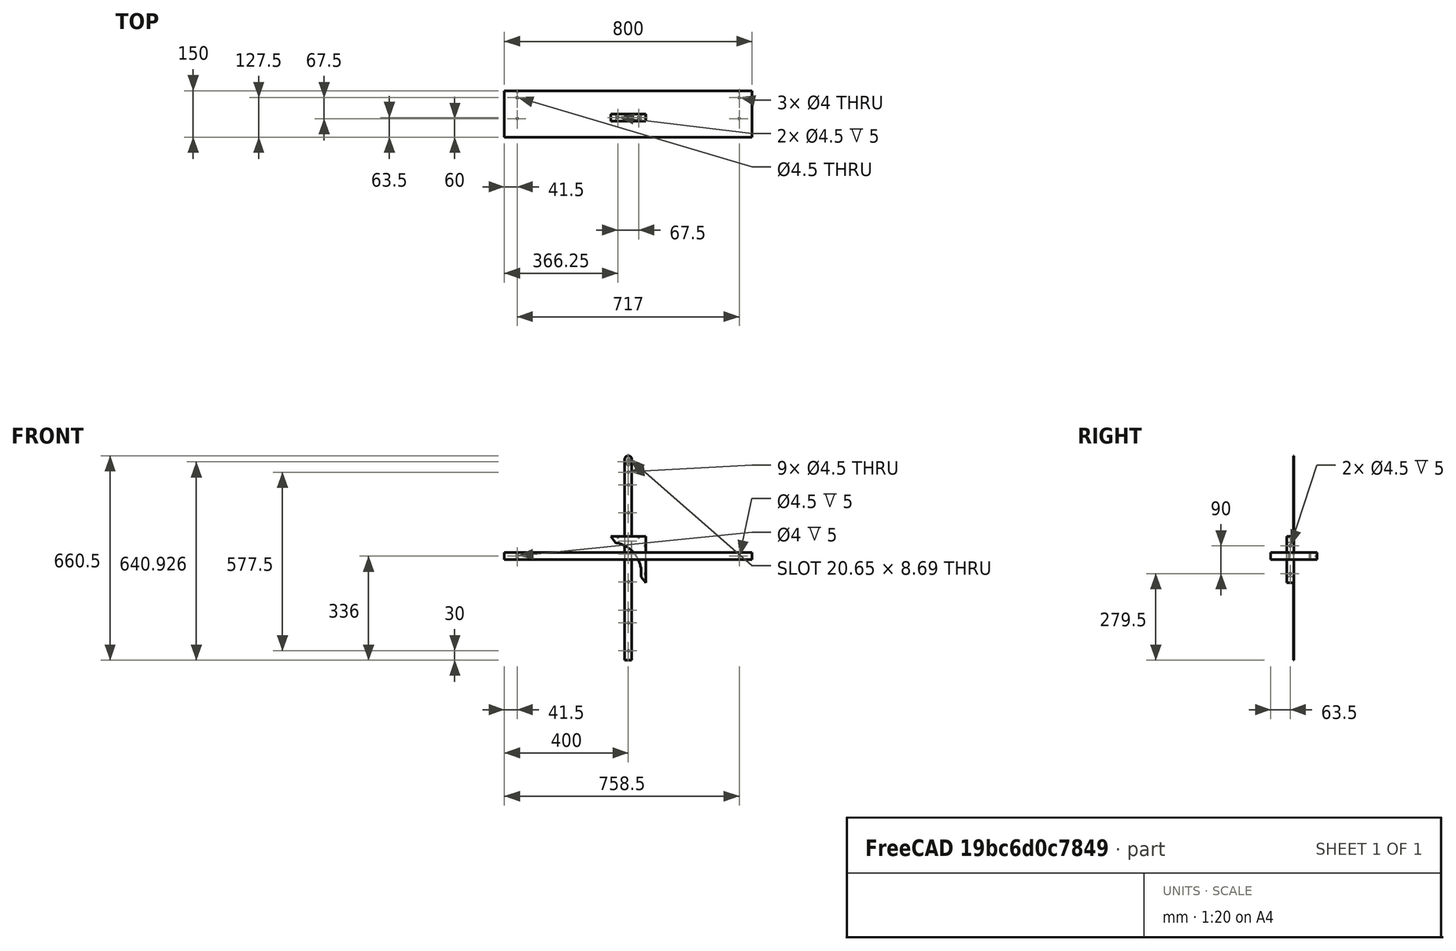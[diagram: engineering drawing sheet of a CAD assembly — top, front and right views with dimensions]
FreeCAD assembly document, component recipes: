
FREECAD ASSEMBLY — COMPONENT RECIPES ("shelf")

This assembly document has 11 components, labeled P0..P10 below (a component is one placed body or linked part). 11 of them carry a construction recipe — the FreeCAD feature program that regenerates the part from scratch, quoted from this document or its linked companion documents; the rest are supplied as boundary geometry only. No exploded tour is included for this assembly.
COMPONENT P0 — recipe-attached ("Plank001", modeled in this document).
Construction recipe (the document's own serialized feature program — sketch geometry with constraints, then the solid features built on it; lengths are millimeters unless a unit is written):

FEATURE [Sketcher::SketchObject] Sketch  label="Top view"
  ArcFitTolerance = 1e-06
  AttachmentSupport = -> [XY_Plane]
  FullyConstrained = true
  MakeInternals = false
  MapMode = 5
  expr: Constraints[12] = <<data>>.pw
  expr: Constraints[13] = <<data>>.pl
  sketch-geometry (6):
    g0: LineSegment StartX=400 StartY=-75 StartZ=0 EndX=400 EndY=75 EndZ=0
    g1: LineSegment StartX=400 StartY=75 StartZ=0 EndX=-400 EndY=75 EndZ=0
    g2: LineSegment StartX=-400 StartY=75 StartZ=0 EndX=-400 EndY=-75 EndZ=0
    g3: LineSegment StartX=-400 StartY=-75 StartZ=0 EndX=400 EndY=-75 EndZ=0
    g4: GeomPoint [constr] X=-2.3e-15 Y=75 Z=0
    g5: GeomPoint [constr] X=400 Y=0 Z=0
  constraints (14):
    c: Coincident(g0,g1)
    c: Coincident(g1,g2)
    c: Coincident(g2,g3)
    c: Coincident(g3,g0)
    c: Vertical(g0)
    c: Vertical(g2)
    c: Horizontal(g1)
    c: Horizontal(g3)
    c: Symmetric(g1,g1,g4)
    c: Symmetric(g0,g0,g5)
    c: Vertical(g4,g-1)
    c: Horizontal(g5,g-1)
    c: DistanceY(g2,g2) = 150
    c: DistanceX(g3,g3) = 800
FEATURE [PartDesign::Pad] Pad
  Direction = (0,0,1)
  Length = 23
  Length2 = 10
  Profile = -> Sketch
  ReferenceAxis = -> Sketch [N_Axis]
  Refine = true
  Suppressed = false
  Type = 0
  expr: Length = <<data>>.pt
FEATURE [Sketcher::SketchObject] Sketch005
  ArcFitTolerance = 1e-06
  AttachmentSupport = -> [Pad]
  ExternalGeometry = -> [Pad]
  FullyConstrained = true
  MakeInternals = false
  MapMode = 5
  Placement = pos=(0,0,23) rot=(0,0,1;0rad)
  expr: Constraints[22] = <<data>>.pw * <<data>>.tr * <<data>>.hr
  expr: Constraints[24] = <<data>>.pw - <<data>>.pw * <<data>>.tr * (1 - <<data>>.hr)
  expr: Constraints[25] = <<data>>.pt / 2 + <<data>>.ts
  expr: Constraints[6] = <<data>>.sd
  sketch-geometry (11):
    g0: GeomPoint [constr] X=-358.5 Y=75 Z=0
    g1: GeomPoint [constr] X=-358.5 Y=-75 Z=0
    g2: LineSegment [constr] StartX=-358.5 StartY=75 StartZ=0 EndX=-358.5 EndY=-75 EndZ=0
    g3: Circle CenterX=-358.5 CenterY=52.5 CenterZ=0 NormalX=0 NormalY=0 NormalZ=1 AngleXU=0 Radius=2.25
    g4: LineSegment [constr] StartX=-400 StartY=75 StartZ=0 EndX=-400 EndY=52.5 EndZ=0
    g5: LineSegment [constr] StartX=-400 StartY=52.5 StartZ=0 EndX=-358.5 EndY=52.5 EndZ=0
    g6: LineSegment [constr] StartX=-358.5 StartY=52.5 StartZ=0 EndX=-358.5 EndY=75 EndZ=0
    g7: LineSegment [constr] StartX=-358.5 StartY=75 StartZ=0 EndX=-400 EndY=75 EndZ=0
    g8: Circle CenterX=-358.5 CenterY=-15 CenterZ=0 NormalX=0 NormalY=0 NormalZ=1 AngleXU=0 Radius=2
    g9: Circle CenterX=358.5 CenterY=-15 CenterZ=0 NormalX=0 NormalY=0 NormalZ=1 AngleXU=0 Radius=2
    g10: Circle CenterX=358.5 CenterY=52.5 CenterZ=0 NormalX=0 NormalY=0 NormalZ=1 AngleXU=0 Radius=2
  constraints (26):
    c: PointOnObject(g0,g-3)
    c: PointOnObject(g1,g-5)
    c: Coincident(g2,g0)
    c: Coincident(g2,g1)
    c: Vertical(g2)
    c: PointOnObject(g3,g2)
    c: Diameter(g3) = 4.5
    c: Coincident(g4,g5)
    c: Coincident(g5,g6)
    c: Coincident(g6,g7)
    c: Coincident(g7,g4)
    c: Vertical(g4)
    c: Vertical(g6)
    c: Horizontal(g5)
    c: Horizontal(g7)
    c: Coincident(g4,g-4)
    c: Coincident(g5,g3)
    c: Diameter(g8) = 4
    c: Diameter(g9) = 4
    c: Symmetric(g9,g8,g-2)
    c: Diameter(g10) = 4
    c: Symmetric(g10,g3,g-2)
    c: DistanceY(g3,g0) = 22.5
    c: PointOnObject(g8,g2)
    c: DistanceY(g-5,g8) = 60
    c: Distance(g5,g5) = 41.5
FEATURE [PartDesign::Pocket] Pocket002
  BaseFeature = -> Pad
  Direction = (0,0,-1)
  Length = 23
  Length2 = 5
  Profile = -> Sketch005
  ReferenceAxis = -> Sketch005 [N_Axis]
  Refine = true
  Suppressed = false
  Type = 0
  expr: Length = <<data>>.pt
FEATURE [Sketcher::SketchObject] Sketch006
  ArcFitTolerance = 1e-06
  AttachmentSupport = -> [Pocket002]
  ExternalGeometry = -> [Pocket002]
  FullyConstrained = true
  MakeInternals = false
  MapMode = 5
  Placement = pos=(0,75,0) rot=(0,0.707107,0.707107;3.14159rad)
  expr: Constraints[11] = <<data>>.sd
  expr: Constraints[14] = <<data>>.pt / 2
  expr: Constraints[9] = <<data>>.pt / 2 + <<data>>.ts
  sketch-geometry (6):
    g0: LineSegment [constr] StartX=-400 StartY=23 StartZ=0 EndX=-400 EndY=11.5 EndZ=0
    g1: LineSegment [constr] StartX=-400 StartY=11.5 StartZ=0 EndX=-358.5 EndY=11.5 EndZ=0
    g2: LineSegment [constr] StartX=-358.5 StartY=11.5 StartZ=0 EndX=-358.5 EndY=23 EndZ=0
    g3: LineSegment [constr] StartX=-358.5 StartY=23 StartZ=0 EndX=-400 EndY=23 EndZ=0
    g4: Circle CenterX=-358.5 CenterY=11.5 CenterZ=0 NormalX=0 NormalY=0 NormalZ=1 AngleXU=0 Radius=2.25
    g5: Circle CenterX=358.5 CenterY=11.5 CenterZ=0 NormalX=0 NormalY=0 NormalZ=1 AngleXU=0 Radius=2
  constraints (15):
    c: Coincident(g0,g1)
    c: Coincident(g1,g2)
    c: Coincident(g2,g3)
    c: Coincident(g3,g0)
    c: Vertical(g0)
    c: Vertical(g2)
    c: Horizontal(g1)
    c: Horizontal(g3)
    c: Coincident(g0,g-4)
    c: DistanceX(g3,g3) = 41.5
    c: Coincident(g4,g1)
    c: Diameter(g4) = 4.5
    c: Diameter(g5) = 4
    c: Symmetric(g1,g5,g-2)
    c: DistanceY(g0,g0) = 11.5
FEATURE [PartDesign::Pocket] Pocket003
  BaseFeature = -> Pocket002
  Direction = (0,-1,2e-16)
  Length = 5
  Length2 = 5
  Profile = -> Sketch006
  ReferenceAxis = -> Sketch006 [N_Axis]
  Refine = true
  Suppressed = false
  Type = 0
FEATURE [PartDesign::Body] Body  label="Plank"
  AllowCompound = false
  Group = -> [Sketch,Pad,Sketch005,Pocket002,Sketch006,Pocket003]
  Origin = -> Origin
  Tip = -> Pocket003
COMPONENT P1 — same part as P0; its construction recipe is shown at P0.
COMPONENT P2 — same part as P0; its construction recipe is shown at P0.
COMPONENT P3 — recipe-attached ("Strip001", modeled in this document).
Construction recipe (the document's own serialized feature program — sketch geometry with constraints, then the solid features built on it; lengths are millimeters unless a unit is written):

FEATURE [Sketcher::SketchObject] Sketch002
  ArcFitTolerance = 1e-06
  AttachmentSupport = -> [XZ_Plane002]
  FullyConstrained = true
  MakeInternals = false
  MapMode = 5
  Placement = pos=(0,0,0) rot=(1,0,0;1.5708rad)
  expr: Constraints[10] = <<data>>.pt
  expr: Constraints[11] = <<data>>.stl + <<data>>.pt * 3 + <<data>>.ps * 2 + <<data>>.tr * <<data>>.ps
  expr: Constraints[17] = <<data>>.sd
  expr: Constraints[18] = <<data>>.stl + <<data>>.pt + <<data>>.ps * <<data>>.tr / 5
  expr: Constraints[20] = <<data>>.sd
  expr: Constraints[21] = <<data>>.thd
  expr: Constraints[23] = <<data>>.thpi
  expr: Constraints[24] = <<data>>.sd
  expr: Constraints[26] = <<data>>.sd
  expr: Constraints[27] = <<data>>.thd
  expr: Constraints[29] = <<data>>.sd
  expr: Constraints[31] = <<data>>.sd
  expr: Constraints[32] = <<data>>.thd
  expr: Constraints[33] = <<data>>.thpi
  expr: Constraints[36] = <<data>>.pt / 2 + <<data>>.ps * <<data>>.tr * <<data>>.hr
  expr: Constraints[38] = <<data>>.sd
  expr: Constraints[39] = <<data>>.pt / 2 + <<data>>.ps * <<data>>.tr * <<data>>.hr
  expr: Constraints[41] = <<data>>.sd
  expr: Constraints[42] = <<data>>.pt / 2 + <<data>>.ps * <<data>>.tr * <<data>>.hr
  expr: Constraints[46] = <<data>>.sd
  expr: Constraints[52] = <<data>>.sd
  expr: Constraints[53] = 10 mm
  sketch-geometry (20):
    g0: LineSegment StartX=-11.5 StartY=324.5 StartZ=0 EndX=-11.5 EndY=-324.5 EndZ=0
    g1: LineSegment StartX=-11.5 StartY=-324.5 StartZ=0 EndX=11.5 EndY=-324.5 EndZ=0
    g2: LineSegment StartX=11.5 StartY=-324.5 StartZ=0 EndX=11.5 EndY=324.5 EndZ=0
    g3: LineSegment [constr] StartX=11.5 StartY=324.5 StartZ=0 EndX=-11.5 EndY=324.5 EndZ=0
    g4: ArcOfCircle CenterX=-4e-16 CenterY=324.5 CenterZ=0 NormalX=0 NormalY=0 NormalZ=1 AngleXU=0 Radius=11.5 StartAngle=0 EndAngle=3.14159
    g5: GeomPoint X=-11.5 Y=0 Z=0
    g6: GeomPoint X=0 Y=-324.5 Z=0
    g7: Circle CenterX=0 CenterY=241.5 CenterZ=0 NormalX=0 NormalY=0 NormalZ=1 AngleXU=0 Radius=2.25
    g8: Circle CenterX=0 CenterY=151.5 CenterZ=0 NormalX=0 NormalY=0 NormalZ=1 AngleXU=0 Radius=2.25
    g9: Circle CenterX=0 CenterY=18.5 CenterZ=0 NormalX=0 NormalY=0 NormalZ=1 AngleXU=0 Radius=2.25
    g10: Circle CenterX=0 CenterY=-71.5 CenterZ=0 NormalX=0 NormalY=0 NormalZ=1 AngleXU=0 Radius=2.25
    g11: Circle CenterX=0 CenterY=-204.5 CenterZ=0 NormalX=0 NormalY=0 NormalZ=1 AngleXU=0 Radius=2.25
    g12: Circle CenterX=0 CenterY=-294.5 CenterZ=0 NormalX=0 NormalY=0 NormalZ=1 AngleXU=0 Radius=2.25
    g13: Circle CenterX=0 CenterY=283 CenterZ=0 NormalX=0 NormalY=0 NormalZ=1 AngleXU=0 Radius=2.25
    g14: Circle CenterX=0 CenterY=60 CenterZ=0 NormalX=0 NormalY=0 NormalZ=1 AngleXU=0 Radius=2.25
    g15: Circle CenterX=0 CenterY=-163 CenterZ=0 NormalX=0 NormalY=0 NormalZ=1 AngleXU=0 Radius=2.25
    g16: ArcOfCircle CenterX=-4e-16 CenterY=324.5 CenterZ=0 NormalX=0 NormalY=0 NormalZ=1 AngleXU=0 Radius=2.25 StartAngle=-1.15e-14 EndAngle=3.14159
    g17: LineSegment StartX=2.25 StartY=324.5 StartZ=0 EndX=2.25 EndY=314.5 EndZ=0
    g18: LineSegment StartX=-2.25 StartY=324.5 StartZ=0 EndX=-2.25 EndY=314.5 EndZ=0
    g19: ArcOfCircle CenterX=0 CenterY=310.603 CenterZ=0 NormalX=0 NormalY=0 NormalZ=1 AngleXU=0 Radius=4.5 StartAngle=2.0944 EndAngle=7.33038
  constraints (54):
    c: Coincident(g0,g1)
    c: Coincident(g1,g2)
    c: Coincident(g2,g3)
    c: Coincident(g3,g0)
    c: Vertical(g0)
    c: Vertical(g2)
    c: Horizontal(g1)
    c: Horizontal(g3)
    c: Coincident(g4,g2)
    c: Tangent(g4,g0) = -1.5708
    c: DistanceX(g1,g1) = 23
    c: DistanceY(g2,g2) = 649
    c: Symmetric(g0,g0,g5)
    c: Symmetric(g1,g1,g6)
    c: Horizontal(g5,g-1)
    c: Vertical(g6,g-1)
    c: PointOnObject(g7,g-2)
    c: Diameter(g7) = 4.5
    c: DistanceY(g7,g4) = 83
    c: PointOnObject(g8,g-2)
    c: Diameter(g8) = 4.5
    c: DistanceY(g8,g7) = 90
    c: PointOnObject(g9,g-2)
    c: DistanceY(g9,g8) = 133
    c: Diameter(g9) = 4.5
    c: PointOnObject(g10,g-2)
    c: Diameter(g10) = 4.5
    c: DistanceY(g10,g9) = 90
    c: PointOnObject(g11,g-2)
    c: Diameter(g11) = 4.5
    c: PointOnObject(g12,g-2)
    c: Diameter(g12) = 4.5
    c: DistanceY(g12,g11) = 90
    c: DistanceY(g11,g10) = 133
    c: PointOnObject(g13,g-2)
    c: Equal(g13,g7)
    c: DistanceY(g7,g13) = 41.5
    c: PointOnObject(g14,g-2)
    c: Diameter(g14) = 4.5
    c: DistanceY(g9,g14) = 41.5
    c: PointOnObject(g15,g-2)
    c: Diameter(g15) = 4.5
    c: DistanceY(g11,g15) = 41.5
    c: Tangent(g16,g17) = 1.5708
    c: Tangent(g16,g18) = -1.5708
    c: Vertical(g18)
    c: Distance(g16,g16) = 4.5
    c: Coincident(g16,g4)
    c: Vertical(g17)
    c: PointOnObject(g19,g-2)
    c: Coincident(g19,g17)
    c: Coincident(g19,g18)
    c: Radius(g19) = 4.5
    c: DistanceY(g17,g16) = 10
FEATURE [PartDesign::Pad] Pad002
  Direction = (0,-1,2e-16)
  Length = 2
  Length2 = 10
  Placement = pos=(0,0,0) rot=(1,0,0;1.5708rad)
  Profile = -> Sketch002
  ReferenceAxis = -> Sketch002 [N_Axis]
  Refine = true
  Suppressed = false
  Type = 0
  expr: Length = <<data>>.strip_thickness
FEATURE [PartDesign::Body] Body002  label="Strip"
  AllowCompound = false
  Group = -> [Sketch002,Pad002]
  Origin = -> Origin002
  Tip = -> Pad002
COMPONENT P4 — same part as P3; its construction recipe is shown at P3.
COMPONENT P5 — recipe-attached ("Triangle001", modeled in this document).
Construction recipe (the document's own serialized feature program — sketch geometry with constraints, then the solid features built on it; lengths are millimeters unless a unit is written):

FEATURE [Sketcher::SketchObject] Sketch001  label="Top view001"
  ArcFitTolerance = 1e-06
  AttachmentSupport = -> [XZ_Plane001]
  FullyConstrained = true
  MakeInternals = false
  MapMode = 5
  Placement = pos=(0,0,0) rot=(1,0,0;1.5708rad)
  expr: Constraints[14] = <<data>>.pw * <<data>>.tr
  expr: Constraints[15] = <<data>>.ps * <<data>>.tr
  sketch-geometry (10):
    g0: LineSegment [constr] StartX=-56.25 StartY=75 StartZ=0 EndX=-56.25 EndY=-75 EndZ=0
    g1: LineSegment [constr] StartX=-56.25 StartY=-75 StartZ=0 EndX=56.25 EndY=-75 EndZ=0
    g2: LineSegment StartX=56.25 StartY=-75 StartZ=0 EndX=56.25 EndY=75 EndZ=0
    g3: LineSegment StartX=56.25 StartY=75 StartZ=0 EndX=-56.25 EndY=75 EndZ=0
    g4: LineSegment [constr] StartX=-56.25 StartY=75 StartZ=0 EndX=56.25 EndY=-75 EndZ=0
    g5: GeomPoint [constr] X=0 Y=75 Z=0
    g6: GeomPoint [constr] X=56.25 Y=0 Z=0
    g7: ArcOfCircle CenterX=-56.25 CenterY=-42.1875 CenterZ=0 NormalX=0 NormalY=0 NormalZ=1 AngleXU=0 Radius=98.3382 StartAngle=6.15252 EndAngle=7.70085
    g8: LineSegment StartX=-56.25 StartY=75 StartZ=0 EndX=-41.25 EndY=55 EndZ=0
    g9: LineSegment StartX=41.25 StartY=-55 StartZ=0 EndX=56.25 EndY=-75 EndZ=0
  constraints (25):
    c: Coincident(g0,g1)
    c: Coincident(g1,g2)
    c: Coincident(g2,g3)
    c: Coincident(g3,g0)
    c: Vertical(g0)
    c: Vertical(g2)
    c: Horizontal(g1)
    c: Horizontal(g3)
    c: Coincident(g4,g0)
    c: Coincident(g4,g1)
    c: Symmetric(g3,g3,g5)
    c: Symmetric(g2,g2,g6)
    c: Vertical(g5,g-1)
    c: Horizontal(g6,g-1)
    c: DistanceX(g3,g3) = 112.5
    c: DistanceY(g2,g2) = 150
    c: PointOnObject(g7,g4)
    c: PointOnObject(g7,g4)
    c: Coincident(g8,g0)
    c: Coincident(g8,g7)
    c: Coincident(g9,g7)
    c: Coincident(g9,g1)
    c: Distance(g9,g9) = 25
    c: Equal(g8,g9)
    c: PointOnObject(g7,g0)
FEATURE [PartDesign::Pad] Pad001
  Direction = (0,-1,2e-16)
  Length = 23
  Length2 = 10
  Placement = pos=(0,0,0) rot=(1,0,0;1.5708rad)
  Profile = -> Sketch001
  ReferenceAxis = -> Sketch001 [N_Axis]
  Refine = true
  Suppressed = false
  Type = 0
  expr: Length = <<data>>.pt
FEATURE [Sketcher::SketchObject] Sketch003
  ArcFitTolerance = 1e-06
  AttachmentSupport = -> [Pad001]
  ExternalGeometry = -> [Pad001]
  FullyConstrained = true
  MakeInternals = false
  MapMode = 5
  Placement = pos=(56.25,0,0) rot=(0.707107,0,0.707107;3.14159rad)
  expr: Constraints[5] = <<data>>.sd
  expr: Constraints[6] = <<data>>.hr * <<data>>.ps * <<data>>.tr
  expr: Constraints[8] = <<data>>.sd
  expr: Constraints[9] = <<data>>.thd
  sketch-geometry (5):
    g0: GeomPoint X=-75 Y=11.5 Z=0
    g1: GeomPoint X=75 Y=11.5 Z=0
    g2: LineSegment [constr] StartX=-75 StartY=11.5 StartZ=0 EndX=75 EndY=11.5 EndZ=0
    g3: Circle CenterX=-45 CenterY=11.5 CenterZ=0 NormalX=0 NormalY=0 NormalZ=1 AngleXU=0 Radius=2.25
    g4: Circle CenterX=45 CenterY=11.5 CenterZ=0 NormalX=0 NormalY=0 NormalZ=1 AngleXU=0 Radius=2.25
  constraints (10):
    c: Symmetric(g-4,g-4,g0)
    c: Symmetric(g-6,g-6,g1)
    c: Coincident(g2,g0)
    c: Coincident(g2,g1)
    c: PointOnObject(g3,g2)
    c: Diameter(g3) = 4.5
    c: Distance(g3,g0) = 30
    c: PointOnObject(g4,g2)
    c: Diameter(g4) = 4.5
    c: DistanceX(g3,g4) = 90
FEATURE [PartDesign::Pocket] Pocket
  BaseFeature = -> Pad001
  Direction = (-1,0,2e-16)
  Length = 5
  Length2 = 5
  Placement = pos=(0,0,0) rot=(1,0,0;1.5708rad)
  Profile = -> Sketch003
  ReferenceAxis = -> Sketch003 [N_Axis]
  Refine = true
  Suppressed = false
  Type = 0
FEATURE [Sketcher::SketchObject] Sketch004
  ArcFitTolerance = 1e-06
  AttachmentSupport = -> [Pocket]
  ExternalGeometry = -> [Pocket]
  FullyConstrained = true
  MakeInternals = false
  MapMode = 5
  Placement = pos=(0,1.67e-14,75) rot=(0,0,1;3.14159rad)
  expr: Constraints[6] = <<data>>.sd
  expr: Constraints[7] = <<data>>.sd
  expr: Constraints[8] = <<data>>.pw * <<data>>.tr * <<data>>.hr
  expr: Constraints[9] = <<data>>.tphd
  sketch-geometry (5):
    g0: GeomPoint X=-56.25 Y=11.5 Z=0
    g1: GeomPoint X=56.25 Y=11.5 Z=0
    g2: LineSegment [constr] StartX=-56.25 StartY=11.5 StartZ=0 EndX=56.25 EndY=11.5 EndZ=0
    g3: Circle CenterX=-33.75 CenterY=11.5 CenterZ=0 NormalX=0 NormalY=0 NormalZ=1 AngleXU=0 Radius=2.25
    g4: Circle CenterX=33.75 CenterY=11.5 CenterZ=0 NormalX=0 NormalY=0 NormalZ=1 AngleXU=0 Radius=2.25
  constraints (10):
    c: Symmetric(g-4,g-4,g0)
    c: Symmetric(g-6,g-6,g1)
    c: Coincident(g2,g0)
    c: Symmetric(g-6,g-6,g2)
    c: PointOnObject(g3,g2)
    c: PointOnObject(g4,g2)
    c: Diameter(g4) = 4.5
    c: Diameter(g3) = 4.5
    c: DistanceX(g0,g3) = 22.5
    c: DistanceX(g3,g4) = 67.5
FEATURE [PartDesign::Pocket] Pocket001
  BaseFeature = -> Pocket
  Direction = (0,0,-1)
  Length = 5
  Length2 = 5
  Placement = pos=(0,0,0) rot=(1,0,0;1.5708rad)
  Profile = -> Sketch004
  ReferenceAxis = -> Sketch004 [N_Axis]
  Refine = true
  Suppressed = false
  Type = 0
FEATURE [PartDesign::Body] Body001  label="Triangle"
  AllowCompound = false
  Group = -> [Sketch001,Pad001,Sketch003,Pocket,Sketch004,Pocket001]
  Origin = -> Origin001
  Tip = -> Pocket001
COMPONENT P6 — same part as P5; its construction recipe is shown at P5.
COMPONENT P7 — same part as P5; its construction recipe is shown at P5.
COMPONENT P8 — same part as P5; its construction recipe is shown at P5.
COMPONENT P9 — same part as P5; its construction recipe is shown at P5.
COMPONENT P10 — same part as P5; its construction recipe is shown at P5.
PROVENANCE & LICENSES
A FreeCAD (.FCStd) document from a public repository crawl; recipes are the document's own serialized feature recipes (and, for linked parts, companion documents' recipes).
License: mit.
